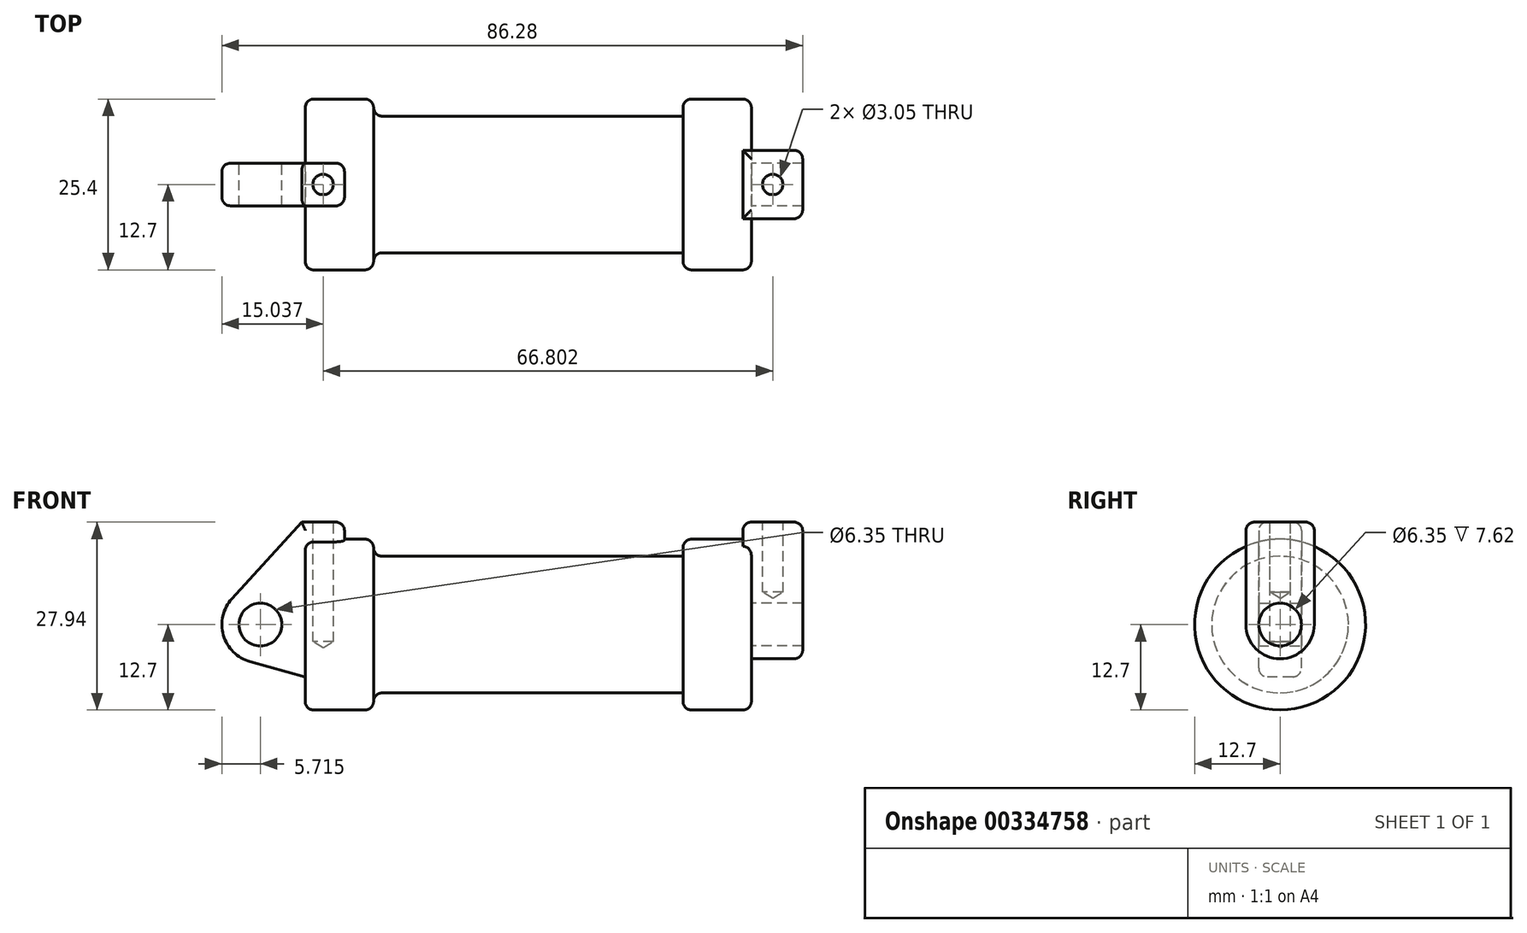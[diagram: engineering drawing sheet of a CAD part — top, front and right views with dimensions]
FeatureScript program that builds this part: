
annotation { "Feature Type Name" : "Feature", "Feature Type Description" : "" }
export const myFeature = defineFeature(function(context is Context, id is Id, definition is map)
    precondition{}
    {
        {
            var Q0;
            Q0=qCreatedBy(makeId("Front.planeOp"),FACE);
            var sketch = newSketch(context, id + "F0", { "sketchPlane" : qUnion([Q0])});
            skLineSegment(sketch, "E0", {"start": v(0, 0) * mm, "end": v(0, 12.7) * mm});
            skLineSegment(sketch, "E1", {"start": v(0, 12.7) * mm, "end": v(10.16, 12.7) * mm});
            skLineSegment(sketch, "E2", {"start": v(10.16, 12.7) * mm, "end": v(10.16, 10.16) * mm});
            skLineSegment(sketch, "E3", {"start": v(10.16, 10.16) * mm, "end": v(56.13, 10.16) * mm});
            skLineSegment(sketch, "E4", {"start": v(56.13, 10.16) * mm, "end": v(56.13, 12.7) * mm});
            skLineSegment(sketch, "E5", {"start": v(56.13, 12.7) * mm, "end": v(66.3, 12.7) * mm});
            skLineSegment(sketch, "E6", {"start": v(66.3, 12.7) * mm, "end": v(66.3, 0) * mm});
            skLineSegment(sketch, "E7", {"start": v(66.3, 0) * mm, "end": v(0, 0) * mm});
            skLineSegment(sketch, "E8", {"start": v(5.84, 15.24) * mm, "end": v(-0.5, 15.24) * mm});
            skLineSegment(sketch, "E9", {"start": v(-0.5, 15.24) * mm, "end": v(-10.88, 3.85) * mm});
            skLineSegment(sketch, "E10", {"start": v(0, 0) * mm, "end": v(-6.65, 0) * mm});
            skCircle(sketch, "E11", {"center": v(-6.65, 0) * mm, "radius": 5.72 * mm});
            skCircle(sketch, "E12", {"center": v(-6.65, 0) * mm, "radius": 3.18 * mm});
            skLineSegment(sketch, "E13", {"start": v(5.84, 15.24) * mm, "end": v(5.84, -9.4) * mm});
            skLineSegment(sketch, "E14", {"start": v(5.84, -9.4) * mm, "end": v(-8.18, -5.5) * mm});
            skSolve(sketch);
        }
        {
            var Q0;
            {var subQ1=sQuery(id+"F0.wireOp",EDGE,"E0");Q0=makeQuery(id+"F0.imprint","IMPRINT",FACE,{"disambiguationData":[TD([[makeQuery(id+"F0.imprint","IMPRINT",EDGE,{"derivedFrom":subQ1}),1.0]])]});}
            var Q1;
            {var subQ5=sQuery(id+"F0.wireOp",EDGE,"E12");Q1=makeQuery(id+"F0.imprint","IMPRINT",FACE,{"disambiguationData":[TD([[makeQuery(id+"F0.imprint","IMPRINT",EDGE,{"derivedFrom":subQ5}),-1.0]])]});}
            var Q2;
            {var subQ0=sQuery(id+"F0.wireOp",EDGE,"E14");Q2=makeQuery(id+"F0.imprint","IMPRINT",FACE,{"disambiguationData":[TD([[makeQuery(id+"F0.imprint","IMPRINT",EDGE,{"derivedFrom":subQ0}),-1.0]])]});}
            var Q3;
            {var subQ0=sQuery(id+"F0.wireOp",EDGE,"E0");Q3=makeQuery(id+"F0.imprint","IMPRINT",FACE,{"disambiguationData":[TD([[makeQuery(id+"F0.imprint","IMPRINT",EDGE,{"derivedFrom":subQ0}),-1.0]])]});}
            extrude(context, id + "F1", {"entities" : qUnion([Q0, Q1, Q2, Q3]), "endBound" : BoundingType.SYMMETRIC, "depth" : 6.35 * mm});
        }
        {
            var Q0;
            {var subQ0=sQuery(id+"F0.wireOp",EDGE,"E0");Q0=makeQuery(id+"F0.imprint","IMPRINT",FACE,{"disambiguationData":[TD([[makeQuery(id+"F0.imprint","IMPRINT",EDGE,{"derivedFrom":subQ0}),-1.0]])]});}
            var Q1;
            {var subQ0=sQuery(id+"F0.wireOp",EDGE,"E2");Q1=makeQuery(id+"F0.imprint","IMPRINT",FACE,{"disambiguationData":[TD([[makeQuery(id+"F0.imprint","IMPRINT",EDGE,{"derivedFrom":subQ0}),-1.0]])]});}
            var Q2;
            Q2=sQuery(id+"F0.wireOp",EDGE,"E7");
            revolve(context, id + "F2", {"operationType" : NewBodyOperationType.ADD, "entities" : qUnion([Q0, Q1]), "axis" : qUnion([Q2]), "revolveType" : RevolveType.FULL});
        }
        {
            var Q0;
            Q0=makeQuery(id+"F2.opRevolve","SWEPT_FACE",FACE,{"disambiguationData":[OSD([sQuery(id+"F0.wireOp",EDGE,"E6")])]});
            var sketch = newSketch(context, id + "F3", { "sketchPlane" : qUnion([Q0])});
            skCircle(sketch, "E15", {"center": v(0, 0) * mm, "radius": 5.08 * mm});
            skCircle(sketch, "E16", {"center": v(0, 0) * mm, "radius": 1.52 * mm});
            skLineSegment(sketch, "E17", {"start": v(-5.08, 0) * mm, "end": v(-5.08, 15.24) * mm});
            skLineSegment(sketch, "E18", {"start": v(-5.08, 15.24) * mm, "end": v(5.08, 15.24) * mm});
            skLineSegment(sketch, "E19", {"start": v(5.08, 15.24) * mm, "end": v(5.08, 0) * mm});
            skSolve(sketch);
        }
        {
            var Q0;
            Q0=makeQuery(id+"F3.imprint","IMPRINT",FACE,{"disambiguationData":[TD([[makeQuery(id+"F3.imprint","IMPRINT",EDGE,{"derivedFrom":sQuery(id+"F3.wireOp",EDGE,"E16")}),-1.0]])]});
            var Q1;
            {var subQ0=sQuery(id+"F3.wireOp",EDGE,"E17");var subQ1=sQuery(id+"F3.wireOp",EDGE,"E15");var subQ2=makeQuery(id+"F3.imprint","INTERSECT",VERTEX,{"derivedFrom":[subQ1,subQ0]});Q1=makeQuery(id+"F3.imprint","IMPRINT",FACE,{"disambiguationData":[TD([[makeQuery(id+"F3.imprint","IMPRINT",EDGE,{"disambiguationData":[TD([[subQ2,1.0]])],"derivedFrom":subQ1}),-1.0]])]});}
            var Q2;
            {var subQ0=sQuery(id+"F3.wireOp",EDGE,"E18");Q2=makeQuery(id+"F3.imprint","IMPRINT",FACE,{"disambiguationData":[TD([[makeQuery(id+"F3.imprint","IMPRINT",EDGE,{"derivedFrom":subQ0}),-1.0]])]});}
            extrude(context, id + "F4", {"entities" : qUnion([Q0, Q1, Q2]), "operationType" : NewBodyOperationType.ADD, "depth" : 7.62 * mm});
        }
        {
            var Q0;
            Q0=makeQuery(id+"F4.opExtrude","CAP_FACE",FACE,{"disambiguationData":[OSD([sQuery(id+"F3.wireOp",EDGE,"E15"),sQuery(id+"F3.wireOp",EDGE,"E16"),sQuery(id+"F3.wireOp",EDGE,"E17"),sQuery(id+"F3.wireOp",EDGE,"E18"),sQuery(id+"F3.wireOp",EDGE,"E19")])],"isStart":true});
            extrude(context, id + "F5", {"entities" : qUnion([Q0]), "operationType" : NewBodyOperationType.ADD, "depth" : 1.27 * mm});
        }
        {
            var Q0;
            Q0=makeQuery(id+"F4.boolean.opBoolean","SPLIT",FACE,{"disambiguationData":[TD([makeQuery(id+"F4.opExtrude","SWEPT_FACE",FACE,{"disambiguationData":[OSD([sQuery(id+"F3.wireOp",EDGE,"E16")])]})])],"derivedFrom":makeQuery(id+"F2.opRevolve","SWEPT_FACE",FACE,{"disambiguationData":[OSD([sQuery(id+"F0.wireOp",EDGE,"E6")])]})});
            var Q1;
            Q1=makeQuery(id+"F4.opExtrude","CAP_FACE",FACE,{"disambiguationData":[OSD([sQuery(id+"F3.wireOp",EDGE,"E15"),sQuery(id+"F3.wireOp",EDGE,"E16"),sQuery(id+"F3.wireOp",EDGE,"E17"),sQuery(id+"F3.wireOp",EDGE,"E18"),sQuery(id+"F3.wireOp",EDGE,"E19")])],"isStart":false});
            extrude(context, id + "F6", {"entities" : qUnion([Q0]), "operationType" : NewBodyOperationType.ADD, "endBound" : BoundingType.UP_TO_SURFACE, "endBoundEntityFace" : qUnion([Q1]), "depth" : 25.4 * mm});
        }
        {
            var Q0;
            Q0=sQuery(id+"F3.wireOp",VERTEX,"E15.center");
            var Q1;
            Q1=makeQuery(id+"F1.opExtrude","SWEPT_BODY",BODY,{"disambiguationData":[OSD([sQuery(id+"F0.wireOp",EDGE,"E8"),sQuery(id+"F0.wireOp",EDGE,"E9"),sQuery(id+"F0.wireOp",EDGE,"E11"),sQuery(id+"F0.wireOp",EDGE,"E12"),sQuery(id+"F0.wireOp",EDGE,"E13"),sQuery(id+"F0.wireOp",EDGE,"E14")])]});
            hole(context, id + "F7", {"style" : HoleStyle.SIMPLE, "endStyle" : HoleEndStyle.THROUGH, "oppositeDirection" : true, "holeDiameter" : 6.35 * mm, "tappedDepth" : 12.7 * mm, "tapClearance" : 3, "startFromSketch" : true, "locations" : qUnion([Q0]), "scope" : qUnion([Q1])});
        }
        {
            var Q0;
            {var subQ0=sQuery(id+"F3.wireOp",EDGE,"E18");Q0=makeQuery(id+"F5.boolean.opBoolean","MERGE",FACE,{"derivedFrom":[makeQuery(id+"F4.opExtrude","SWEPT_FACE",FACE,{"disambiguationData":[OSD([subQ0])]}),makeQuery(id+"F5.opExtrude","SWEPT_FACE",FACE,{"disambiguationData":[OSD([subQ0])]})]});}
            var sketch = newSketch(context, id + "F8", { "sketchPlane" : qUnion([Q0])});
            skLineSegment(sketch, "E20", {"start": v(73.91, 0) * mm, "end": v(65.02, 0) * mm, "construction": true});
            skLineSegment(sketch, "E21", {"start": v(69.47, 5.08) * mm, "end": v(69.47, 0) * mm, "construction": true});
            skSolve(sketch);
        }
        {
            var Q0;
            Q0=makeQuery(id+"F1.opExtrude","SWEPT_FACE",FACE,{"disambiguationData":[OSD([sQuery(id+"F0.wireOp",EDGE,"E8")])]});
            var sketch = newSketch(context, id + "F9", { "sketchPlane" : qUnion([Q0])});
            skLineSegment(sketch, "E22", {"start": v(-0.5, 0) * mm, "end": v(5.84, 0) * mm, "construction": true});
            skLineSegment(sketch, "E23", {"start": v(2.67, 3.18) * mm, "end": v(2.67, 0) * mm, "construction": true});
            skSolve(sketch);
        }
        {
            var Q0;
            Q0=sQuery(id+"F9.wireOp",VERTEX,"E23.end");
            var Q1;
            Q1=makeQuery(id+"F2.opRevolve","SWEPT_BODY",BODY,{"disambiguationData":[OSD([sQuery(id+"F0.wireOp",EDGE,"E0"),sQuery(id+"F0.wireOp",EDGE,"E1"),sQuery(id+"F0.wireOp",EDGE,"E2"),sQuery(id+"F0.wireOp",EDGE,"E3"),sQuery(id+"F0.wireOp",EDGE,"E4"),sQuery(id+"F0.wireOp",EDGE,"E5"),sQuery(id+"F0.wireOp",EDGE,"E6"),sQuery(id+"F0.wireOp",EDGE,"E7")])]});
            var Q2;
            Q2=makeQuery(id+"F1.opExtrude","SWEPT_BODY",BODY,{"disambiguationData":[OSD([sQuery(id+"F0.wireOp",EDGE,"E0"),sQuery(id+"F0.wireOp",EDGE,"E1"),sQuery(id+"F0.wireOp",EDGE,"E7"),sQuery(id+"F0.wireOp",EDGE,"E8"),sQuery(id+"F0.wireOp",EDGE,"E9"),sQuery(id+"F0.wireOp",EDGE,"E11"),sQuery(id+"F0.wireOp",EDGE,"E12"),sQuery(id+"F0.wireOp",EDGE,"E13"),sQuery(id+"F0.wireOp",EDGE,"E14")])]});
            hole(context, id + "F10", {"style" : HoleStyle.SIMPLE, "endStyle" : HoleEndStyle.BLIND, "holeDiameter" : 3.05 * mm, "holeDepth" : 17.78 * mm, "tappedDepth" : 12.7 * mm, "tapClearance" : 3, "startFromSketch" : true, "locations" : qUnion([Q0]), "scope" : qUnion([Q1, Q2])});
        }
        {
            var Q0;
            Q0=sQuery(id+"F8.wireOp",VERTEX,"E21.end");
            var Q1;
            Q1=makeQuery(id+"F1.opExtrude","SWEPT_BODY",BODY,{"disambiguationData":[OSD([sQuery(id+"F0.wireOp",EDGE,"E8"),sQuery(id+"F0.wireOp",EDGE,"E9"),sQuery(id+"F0.wireOp",EDGE,"E11"),sQuery(id+"F0.wireOp",EDGE,"E12"),sQuery(id+"F0.wireOp",EDGE,"E13"),sQuery(id+"F0.wireOp",EDGE,"E14")])]});
            hole(context, id + "F11", {"style" : HoleStyle.SIMPLE, "endStyle" : HoleEndStyle.BLIND, "holeDiameter" : 3.05 * mm, "holeDepth" : 10.4 * mm, "tappedDepth" : 12.7 * mm, "tapClearance" : 3, "startFromSketch" : true, "locations" : qUnion([Q0]), "scope" : qUnion([Q1])});
        }
        {
            var Q0;
            {var subQ0=sQuery(id+"F0.wireOp",EDGE,"E5");var subQ1=sQuery(id+"F0.wireOp",EDGE,"E6");Q0=makeQuery(id+"F4.boolean.opBoolean","SPLIT",EDGE,{"disambiguationData":[topologyDisambiguationEdgeConnected([makeQuery(id+"F2.opRevolve","SWEPT_FACE",FACE,{"disambiguationData":[OSD([subQ1])]})])],"derivedFrom":makeQuery(id+"F2.opRevolve","SWEPT_EDGE",EDGE,{"disambiguationData":[OSD([subQ0,subQ1])]})});}
            var Q1;
            Q1=makeQuery(id+"F2.opRevolve","SWEPT_EDGE",EDGE,{"disambiguationData":[OSD([sQuery(id+"F0.wireOp",EDGE,"E4"),sQuery(id+"F0.wireOp",EDGE,"E5")])]});
            var Q2;
            Q2=makeQuery(id+"F2.opRevolve","SWEPT_EDGE",EDGE,{"disambiguationData":[OSD([sQuery(id+"F0.wireOp",EDGE,"E2"),sQuery(id+"F0.wireOp",EDGE,"E3")])]});
            var Q3;
            Q3=makeQuery(id+"F2.opRevolve","SWEPT_EDGE",EDGE,{"disambiguationData":[OSD([sQuery(id+"F0.wireOp",EDGE,"E1"),sQuery(id+"F0.wireOp",EDGE,"E2")])]});
            var Q4;
            Q4=makeQuery(id+"F2.opRevolve","SWEPT_EDGE",EDGE,{"disambiguationData":[OSD([sQuery(id+"F0.wireOp",EDGE,"E0"),sQuery(id+"F0.wireOp",EDGE,"E1")])]});
            var Q5;
            Q5=makeQuery(id+"F4.opExtrude","CAP_EDGE",EDGE,{"disambiguationData":[OSD([sQuery(id+"F3.wireOp",EDGE,"E17")])],"isStart":false});
            var Q6;
            {var subQ0=sQuery(id+"F3.wireOp",EDGE,"E17");Q6=makeQuery(id+"F4.boolean.opBoolean","SPLIT",EDGE,{"disambiguationData":[topologyDisambiguationEdgeConnected([makeQuery(id+"F2.opRevolve","SWEPT_FACE",FACE,{"disambiguationData":[OSD([sQuery(id+"F0.wireOp",EDGE,"E6")])]})])],"derivedFrom":makeQuery(id+"F4.opExtrude","CAP_EDGE",EDGE,{"disambiguationData":[OSD([subQ0])],"isStart":true})});}
            var Q7;
            Q7=makeQuery(id+"F4.opExtrude","SWEPT_EDGE",EDGE,{"disambiguationData":[OSD([sQuery(id+"F3.wireOp",EDGE,"E15"),sQuery(id+"F3.wireOp",EDGE,"E17")])]});
            var Q8;
            {var subQ0=sQuery(id+"F3.wireOp",EDGE,"E18");var subQ1=sQuery(id+"F3.wireOp",EDGE,"E17");Q8=makeQuery(id+"F5.boolean.opBoolean","MERGE",EDGE,{"derivedFrom":[makeQuery(id+"F4.opExtrude","SWEPT_EDGE",EDGE,{"disambiguationData":[OSD([subQ1,subQ0])]}),makeQuery(id+"F5.opExtrude","SWEPT_EDGE",EDGE,{"disambiguationData":[OSD([subQ1,subQ0])]})]});}
            var Q9;
            Q9=makeQuery(id+"F4.opExtrude","CAP_EDGE",EDGE,{"disambiguationData":[OSD([sQuery(id+"F3.wireOp",EDGE,"E18")])],"isStart":false});
            var Q10;
            {var subQ0=sQuery(id+"F3.wireOp",EDGE,"E19");var subQ1=sQuery(id+"F3.wireOp",EDGE,"E18");Q10=makeQuery(id+"F5.boolean.opBoolean","MERGE",EDGE,{"derivedFrom":[makeQuery(id+"F4.opExtrude","SWEPT_EDGE",EDGE,{"disambiguationData":[OSD([subQ1,subQ0])]}),makeQuery(id+"F5.opExtrude","SWEPT_EDGE",EDGE,{"disambiguationData":[OSD([subQ1,subQ0])]})]});}
            var Q11;
            Q11=makeQuery(id+"F5.opExtrude","CAP_EDGE",EDGE,{"disambiguationData":[OSD([sQuery(id+"F3.wireOp",EDGE,"E18")])],"isStart":false});
            var Q12;
            {var subQ0=sQuery(id+"F0.wireOp",EDGE,"E13");Q12=makeQuery(id+"F1.opExtrude","CAP_EDGE",EDGE,{"disambiguationData":[OSD([subQ0]),TDD([makeQuery(id+"F0.imprint","IMPRINT",EDGE,{"disambiguationData":[TD([[makeQuery(id+"F0.imprint","INTERSECT",VERTEX,{"derivedFrom":[sQuery(id+"F0.wireOp",EDGE,"E8"),subQ0]}),-1.0]])],"derivedFrom":subQ0})])],"isStart":false});}
            var Q13;
            {var subQ0=sQuery(id+"F0.wireOp",EDGE,"E13");Q13=makeQuery(id+"F1.opExtrude","CAP_EDGE",EDGE,{"disambiguationData":[OSD([subQ0]),TDD([makeQuery(id+"F0.imprint","IMPRINT",EDGE,{"disambiguationData":[TD([[makeQuery(id+"F0.imprint","INTERSECT",VERTEX,{"derivedFrom":[sQuery(id+"F0.wireOp",EDGE,"E8"),subQ0]}),-1.0]])],"derivedFrom":subQ0})])],"isStart":true});}
            var Q14;
            Q14=makeQuery(id+"F1.opExtrude","SWEPT_EDGE",EDGE,{"disambiguationData":[OSD([sQuery(id+"F0.wireOp",EDGE,"E8"),sQuery(id+"F0.wireOp",EDGE,"E13")])]});
            var Q15;
            Q15=makeQuery(id+"F1.opExtrude","SWEPT_EDGE",EDGE,{"disambiguationData":[OSD([sQuery(id+"F0.wireOp",EDGE,"E1"),sQuery(id+"F0.wireOp",EDGE,"E13")])]});
            var Q16;
            Q16=makeQuery(id+"F1.opExtrude","CAP_EDGE",EDGE,{"disambiguationData":[OSD([sQuery(id+"F0.wireOp",EDGE,"E8")])],"isStart":false});
            var Q17;
            Q17=makeQuery(id+"F1.opExtrude","CAP_EDGE",EDGE,{"disambiguationData":[OSD([sQuery(id+"F0.wireOp",EDGE,"E8")])],"isStart":true});
            var Q18;
            Q18=makeQuery(id+"F1.opExtrude","CAP_EDGE",EDGE,{"disambiguationData":[OSD([sQuery(id+"F0.wireOp",EDGE,"E9")])],"isStart":false});
            var Q19;
            Q19=makeQuery(id+"F1.opExtrude","CAP_EDGE",EDGE,{"disambiguationData":[OSD([sQuery(id+"F0.wireOp",EDGE,"E9")])],"isStart":true});
            var Q20;
            Q20=makeQuery(id+"F1.opExtrude","SWEPT_EDGE",EDGE,{"disambiguationData":[OSD([sQuery(id+"F0.wireOp",EDGE,"E9"),sQuery(id+"F0.wireOp",EDGE,"E11")])]});
            var Q21;
            Q21=makeQuery(id+"F1.opExtrude","CAP_EDGE",EDGE,{"disambiguationData":[OSD([sQuery(id+"F0.wireOp",EDGE,"E11")])],"isStart":true});
            var Q22;
            Q22=makeQuery(id+"F1.opExtrude","CAP_EDGE",EDGE,{"disambiguationData":[OSD([sQuery(id+"F0.wireOp",EDGE,"E14")])],"isStart":true});
            var Q23;
            Q23=makeQuery(id+"F1.opExtrude","CAP_EDGE",EDGE,{"disambiguationData":[OSD([sQuery(id+"F0.wireOp",EDGE,"E14")])],"isStart":false});
            var Q24;
            Q24=makeQuery(id+"F1.opExtrude","CAP_EDGE",EDGE,{"disambiguationData":[OSD([sQuery(id+"F0.wireOp",EDGE,"E11")])],"isStart":false});
            fillet(context, id + "F12", {"entities" : qUnion([Q0, Q1, Q2, Q3, Q4, Q5, Q6, Q7, Q8, Q9, Q10, Q11, Q12, Q13, Q14, Q15, Q16, Q17, Q18, Q19, Q20, Q21, Q22, Q23, Q24]), "radius" : 1.27 * mm, "tangentPropagation" : true, "allowEdgeOverflow" : false});
        }
    });
